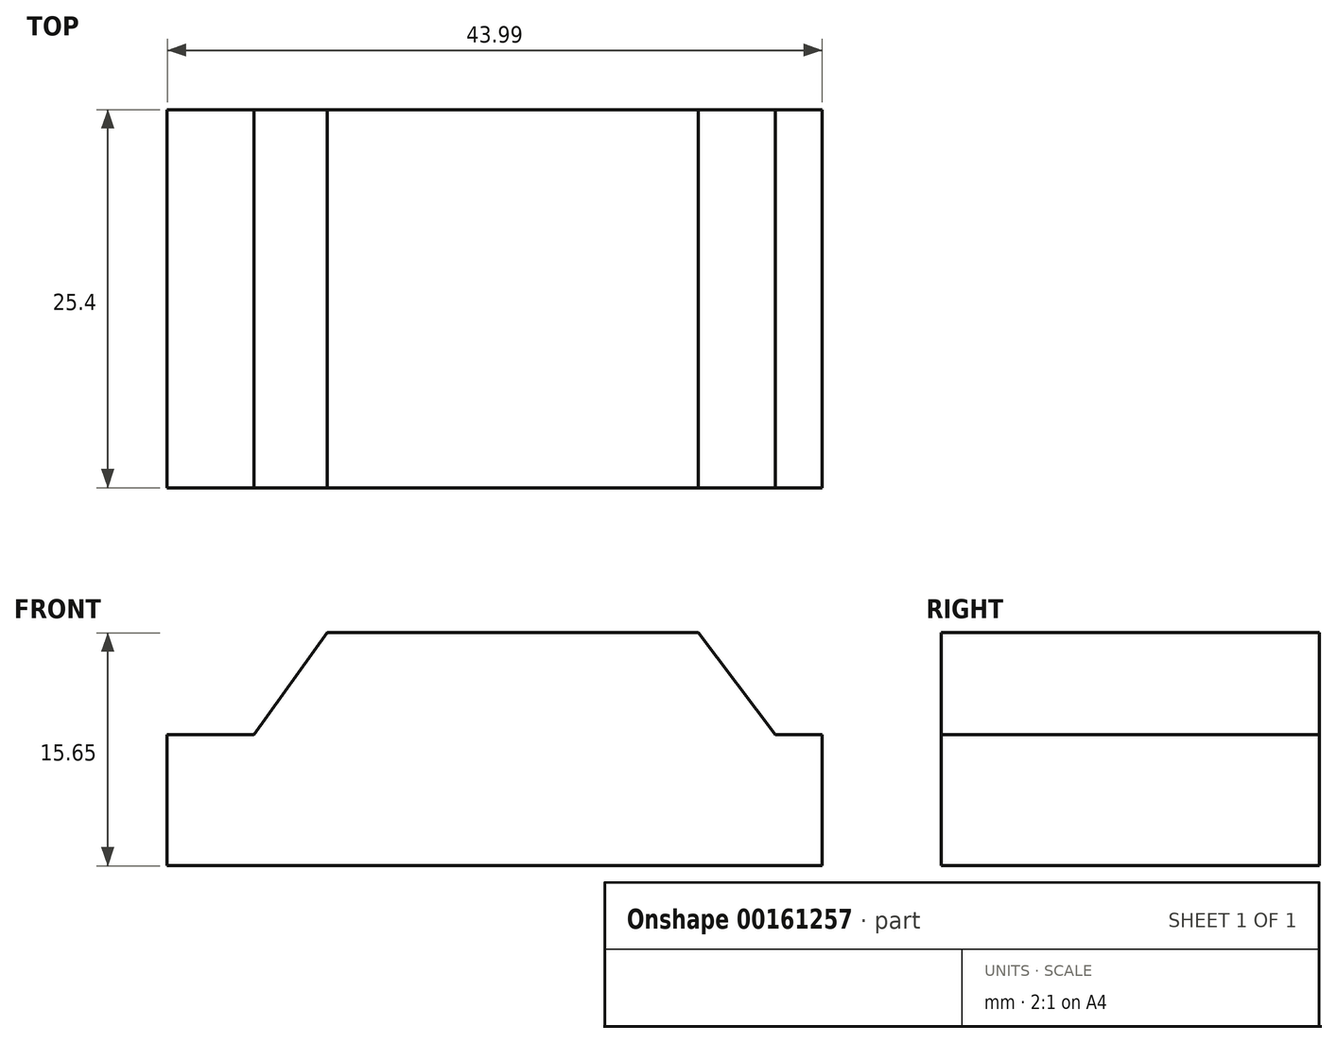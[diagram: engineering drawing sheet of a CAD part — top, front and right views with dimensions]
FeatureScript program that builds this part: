
annotation { "Feature Type Name" : "Feature", "Feature Type Description" : "" }
export const myFeature = defineFeature(function(context is Context, id is Id, definition is map)
    precondition{}
    {
        {
            var Q0;
            Q0=qCreatedBy(makeId("Front.planeOp"),FACE);
            var sketch = newSketch(context, id + "F0", { "sketchPlane" : qUnion([Q0])});
            skLineSegment(sketch, "E0.bottom", {"start": v(-18.51, 4.5) * mm, "end": v(25.48, 4.5) * mm});
            skLineSegment(sketch, "E0.top", {"start": v(-18.51, -4.3) * mm, "end": v(25.48, -4.3) * mm});
            skLineSegment(sketch, "E0.left", {"start": v(-18.51, 4.5) * mm, "end": v(-18.51, -4.3) * mm});
            skLineSegment(sketch, "E0.right", {"start": v(25.48, 4.5) * mm, "end": v(25.48, -4.3) * mm});
            skSolve(sketch);
        }
        {
            var Q0;
            Q0=makeQuery(id+"F0.imprint","IMPRINT",FACE,{"disambiguationData":[TD([[makeQuery(id+"F0.imprint","IMPRINT",EDGE,{"derivedFrom":sQuery(id+"F0.wireOp",EDGE,"E0.bottom")}),-1.0]])]});
            extrude(context, id + "F1", {"entities" : qUnion([Q0]), "depth" : 25.4 * mm});
        }
        {
            var Q0;
            Q0=makeQuery(id+"F1.opExtrude","CAP_FACE",FACE,{"disambiguationData":[OSD([sQuery(id+"F0.wireOp",EDGE,"E0.bottom"),sQuery(id+"F0.wireOp",EDGE,"E0.top"),sQuery(id+"F0.wireOp",EDGE,"E0.left"),sQuery(id+"F0.wireOp",EDGE,"E0.right")])],"isStart":false});
            var sketch = newSketch(context, id + "F2", { "sketchPlane" : qUnion([Q0])});
            skLineSegment(sketch, "E1", {"start": v(-12.7, 4.5) * mm, "end": v(-7.76, 11.34) * mm});
            skLineSegment(sketch, "E2", {"start": v(-7.76, 11.34) * mm, "end": v(17.15, 11.34) * mm});
            skLineSegment(sketch, "E3", {"start": v(17.15, 11.34) * mm, "end": v(22.33, 4.5) * mm});
            skSolve(sketch);
        }
        {
            var Q0;
            {var subQ0=sQuery(id+"F2.wireOp",EDGE,"E1");Q0=makeQuery(id+"F2.imprint","IMPRINT",FACE,{"disambiguationData":[TD([[makeQuery(id+"F2.imprint","IMPRINT",EDGE,{"derivedFrom":subQ0}),-1.0]])]});}
            extrude(context, id + "F3", {"entities" : qUnion([Q0]), "operationType" : NewBodyOperationType.ADD, "oppositeDirection" : true, "depth" : 25.4 * mm});
        }
    });
